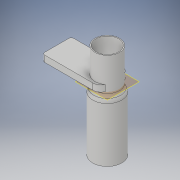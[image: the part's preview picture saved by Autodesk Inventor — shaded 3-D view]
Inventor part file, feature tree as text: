
AUTODESK INVENTOR PART (.ipt)
format: ipt  version: 2019 (Build 230136000, 136)  size: 166,912 bytes
history: native  units: mm
features: extrude x4, sketch x4, fillet x2, plane x1
ambient origin geometry x8: Origin, YZ Plane, XZ Plane, XY Plane, X Axis, Y Axis, Z Axis, Center Point
bodies: Solid1 (feature_tree)
feature tree (11):
  extrude  "Extrusion1"  Depth=23.0mm
  extrude  "Extrusion2"  Depth=19.5mm
  extrude  "Extrusion3"  Depth=5.0mm TaperAngle=0.0deg
  fillet  "Fillet1"  Radius=5.0mm
  fillet  "Fillet2"  Radius=5.0mm
  plane  "Work Plane1"
  extrude  "Extrusion5"  Depth=40.0mm
  sketch  "Sketch1"  dims[d0=20.0mm d1=23.0mm]
  sketch  "Sketch2"  dims[d2=40.0mm d3=0.0mm d4=19.5mm]
  sketch  "Sketch3"  dims[d5=35.0mm d6=0.0mm d7=5.0mm d8=0.0mm d9=5.0mm d10=5.0mm]
  sketch  "Sketch4"  dims[d11=50.0mm d19=40.0mm d20=2.0mm d21=5.0mm d22=0.0mm]
